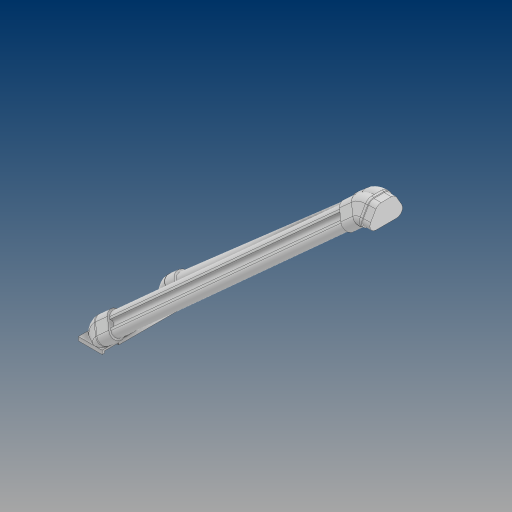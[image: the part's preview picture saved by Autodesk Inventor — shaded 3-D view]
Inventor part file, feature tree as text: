
AUTODESK INVENTOR PART (.ipt)
format: ipt  version: 2023 (Build 270158000, 158)  size: 502,272 bytes
history: native  units: mm
features: sketch x13, extrude x10, revolve x4, plane x2, mirror x1, fillet x1
ambient origin geometry x8: Origin, YZ Plane, XZ Plane, XY Plane, X Axis, Y Axis, Z Axis, Center Point
bodies: Solid1 (feature_tree)
feature tree (31):
  sketch  "Sketch1"  dims[d0=25.0mm d1=50.0mm]
  revolve  "Revolution1"  [1 undecoded]
  sketch  "Sketch2"  dims[d2=7.5mm d4=15.0mm]
  plane  "Work Plane1"
  sketch  "Sketch4"  dims[d5=11.0mm d6=11.0mm]
  plane  "Work Plane2"
  sketch  "Sketch5"  dims[d7=60.0deg d8=11.0mm]
  revolve  "Revolution2"  [1 undecoded]
  sketch  "Sketch6"  dims[d9=15.0mm d10=45.0deg]
  extrude  "Extrusion2"  Depth=11.0mm
  extrude  "Extrusion3"  Depth=11.0mm
  sketch  "Sketch7"  dims[d11=90.0deg d12=150.0deg]
  revolve  "Revolution3"  Angle=45.0deg
  revolve  "Revolution4"  Angle=150.0deg
  extrude  "Extrusion7"  Depth=39.75mm
  extrude  "Extrusion8"  Depth=15.0mm
  mirror  "Mirror1"
  sketch  "Sketch12"  dims[d15=12.73686mm d20=15.0mm]
  sketch  "Sketch15"  dims[d21=11.0mm d22=90.0deg]
  extrude  "Extrusion12"  TaperAngle=90.0deg  [1 undecoded]
  extrude  "Extrusion13"  TaperAngle=0.0deg  [1 undecoded]
  extrude  "Extrusion14"  TaperAngle=0.0deg  [1 undecoded]
  sketch  "Sketch16"  dims[d23=12.736803mm d24=0.0mm]
  extrude  "Extrusion15"  Depth=1.134464mm
  extrude  "Extrusion16"  Depth=10.0mm
  extrude  "Extrusion17"  Depth=10.0mm
  fillet  "Fillet2"  Radius=2.0mm
  sketch  "Sketch20"  dims[d39=11.0mm d40=11.0mm d41=2.0mm d42=2.0mm d43=2.0mm d44=2.0mm d47=6.5mm d48=2.0mm d49=0.0mm d50=321.5mm d51=0.0mm d52=11.0mm d53=11.0mm d54=6.5mm d55=6.5mm d56=15.0mm d57=7.5mm d58=60.0deg d59=7.5mm d60=90.0deg d61=1.134464mm d62=15.0mm d63=15.0mm d64=11.0mm d65=11.0mm d66=7.5mm d67=120.0deg d68=7.5mm d69=90.0deg d70=7.5mm d71=120.0deg d72=45.0deg d114=275.0mm d115=100.0mm d116=50.0mm d122=15.0mm d123=0.0mm d124=15.0mm d125=0.0mm d143=25.0mm d144=100.0mm d145=10.0mm d146=90.0deg d147=12.736803mm d148=90.0deg d149=15.0mm d150=5.5mm d151=7.5mm d152=7.5mm d153=2.0mm d154=0.0mm d155=12.0mm d156=0.0mm d157=1.0mm d158=0.0mm d166=550.0mm d167=300.0mm d168=20.0mm d169=15.0mm d170=15.0mm d171=15.0mm d172=15.0mm d173=15.0mm d174=7.5mm d175=7.5mm d176=7.5mm d177=15.0mm d178=35.0mm d179=0.0mm d180=100.0mm d181=0.0mm d182=15.0mm d183=15.0mm d184=15.0mm d185=15.0mm d186=7.5mm d187=7.5mm d188=1.1mm d189=7.6mm d190=0.0mm d193=0.75mm d194=50.0mm d195=100.0mm d196=300.0mm d198=20.0mm d201=10.0mm d202=2.0mm d241=0.5mm d242=0.5mm d265=70.0mm d267=15.0mm d268=15.0mm d269=15.0mm d270=15.0mm d271=12.8mm d272=12.8mm d273=12.8mm d274=1.0mm d275=1.0mm d276=2.0mm d277=30.0mm d278=2.0mm d279=30.0mm d280=2.0mm d281=40.595mm d282=2.5mm d34=0.5mm d35=0.872665mm d36=0.5mm d37=0.872665mm d90=0.5mm d91=0.872665mm d92=0.5mm d93=0.872665mm d160=0.5mm d161=0.872665mm d162=0.5mm d163=0.872665mm d191=0.5mm d192=0.872665mm d213=0.5mm d214=0.872665mm d215=0.5mm d216=0.872665mm]
  sketch  "Sketch8"  dims[d13=20.5mm d14=39.75mm]
  sketch  "Sketch17"  dims[d25=3.59315mm d26=0.0mm]
  sketch  "Sketch18"  dims[d27=15.0mm d28=1.134464mm]
note: 5 required parameter values undecoded (feature->parameter linkage not recoverable at this tier; creation-order binding heuristic only, values carry confidence <= 0.55)